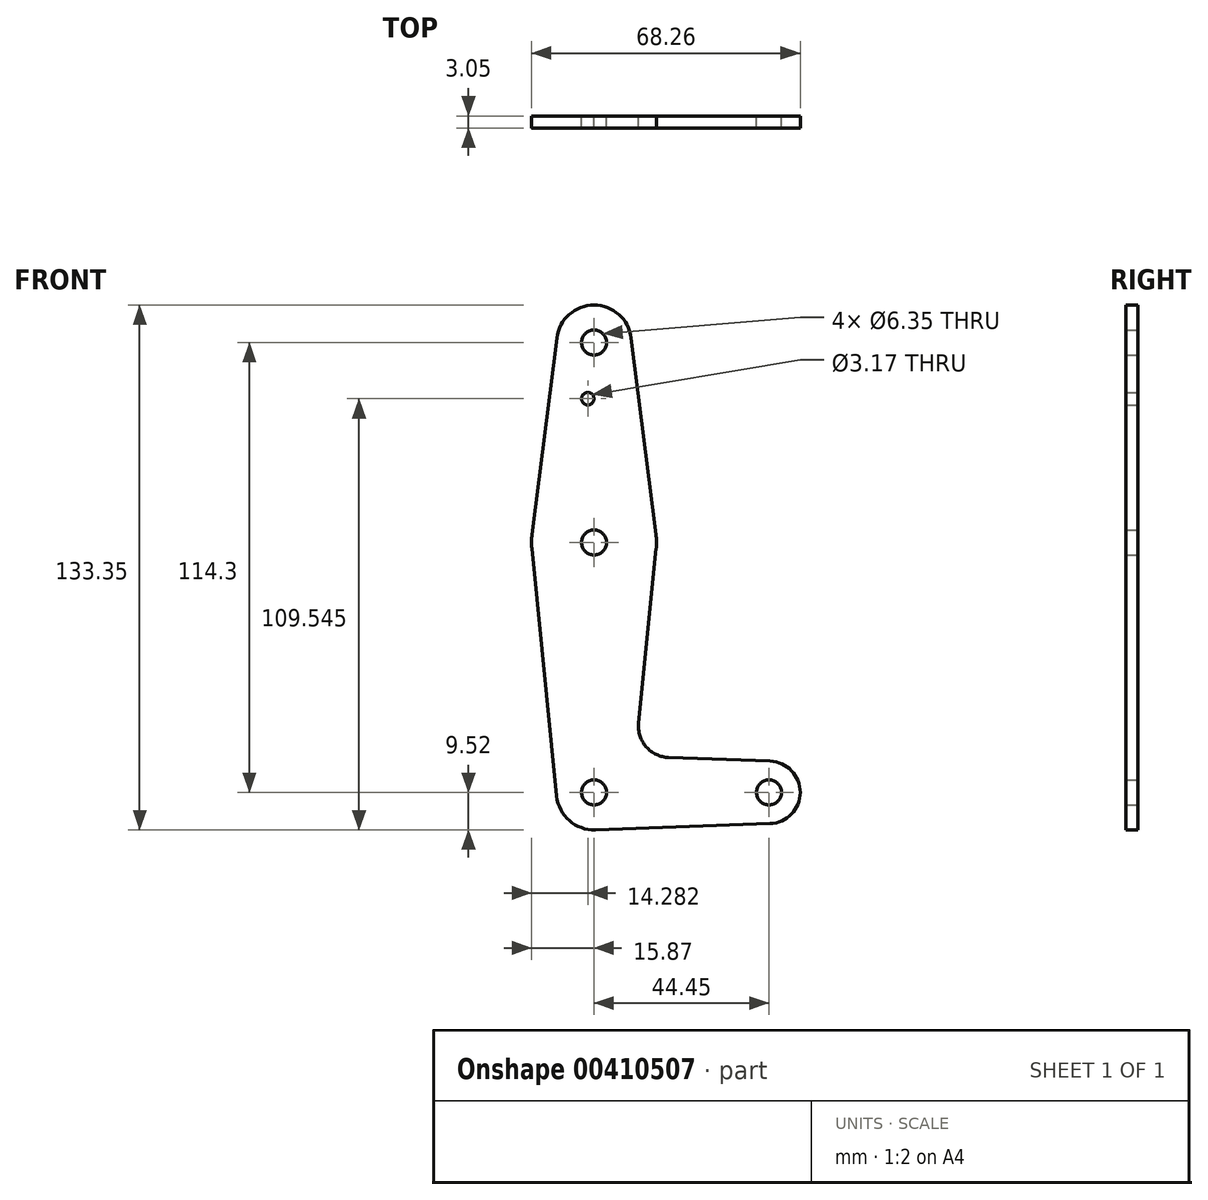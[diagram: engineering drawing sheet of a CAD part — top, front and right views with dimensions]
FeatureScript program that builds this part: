
annotation { "Feature Type Name" : "Feature", "Feature Type Description" : "" }
export const myFeature = defineFeature(function(context is Context, id is Id, definition is map)
    precondition{}
    {
        {
            var Q0;
            Q0=qCreatedBy(makeId("Front.planeOp"),FACE);
            var sketch = newSketch(context, id + "F0", { "sketchPlane" : qUnion([Q0])});
            skLineSegment(sketch, "E0", {"start": v(0, 114.3) * mm, "end": v(0, 0) * mm, "construction": true});
            skLineSegment(sketch, "E1", {"start": v(0, 0) * mm, "end": v(44.45, 0) * mm, "construction": true});
            skCircle(sketch, "E2", {"center": v(44.45, 0) * mm, "radius": 7.94 * mm});
            skCircle(sketch, "E3", {"center": v(0, 0) * mm, "radius": 9.53 * mm});
            skCircle(sketch, "E4", {"center": v(0, 63.5) * mm, "radius": 15.88 * mm});
            skCircle(sketch, "E5", {"center": v(0, 114.3) * mm, "radius": 9.53 * mm});
            skLineSegment(sketch, "E6", {"start": v(-9.45, 115.5) * mm, "end": v(-24, 0) * mm});
            skLineSegment(sketch, "E7", {"start": v(-15.8, 61.91) * mm, "end": v(-9.48, -0.95) * mm});
            skLineSegment(sketch, "E8", {"start": v(15.8, 61.91) * mm, "end": v(11.34, 17.6) * mm});
            skLineSegment(sketch, "E9", {"start": v(18.97, 8.85) * mm, "end": v(44.73, 7.93) * mm});
            skLineSegment(sketch, "E10", {"start": v(44.73, -7.93) * mm, "end": v(0.34, -9.52) * mm});
            skArc(sketch, "E11.filletArc", {"start": v(11.34, 17.6) * mm, "mid": v(13.26, 11.57) * mm, "end": v(18.97, 8.85) * mm});
            skCircle(sketch, "E12", {"center": v(0, 114.3) * mm, "radius": 3.18 * mm});
            skCircle(sketch, "E13", {"center": v(0, 63.5) * mm, "radius": 3.18 * mm});
            skCircle(sketch, "E14", {"center": v(0, 0) * mm, "radius": 3.18 * mm});
            skCircle(sketch, "E15", {"center": v(44.45, 0) * mm, "radius": 3.18 * mm});
            skCircle(sketch, "E16", {"center": v(-1.59, 100.03) * mm, "radius": 1.59 * mm});
            skLineSegment(sketch, "E17", {"start": v(9.45, 115.5) * mm, "end": v(15.75, 65.48) * mm});
            skSolve(sketch);
        }
        {
            var Q0;
            Q0 = qSketchRegion(id + "F0", true);
            extrude(context, id + "F1", {"entities" : qUnion([Q0]), "depth" : 3.05 * mm});
        }
    });
